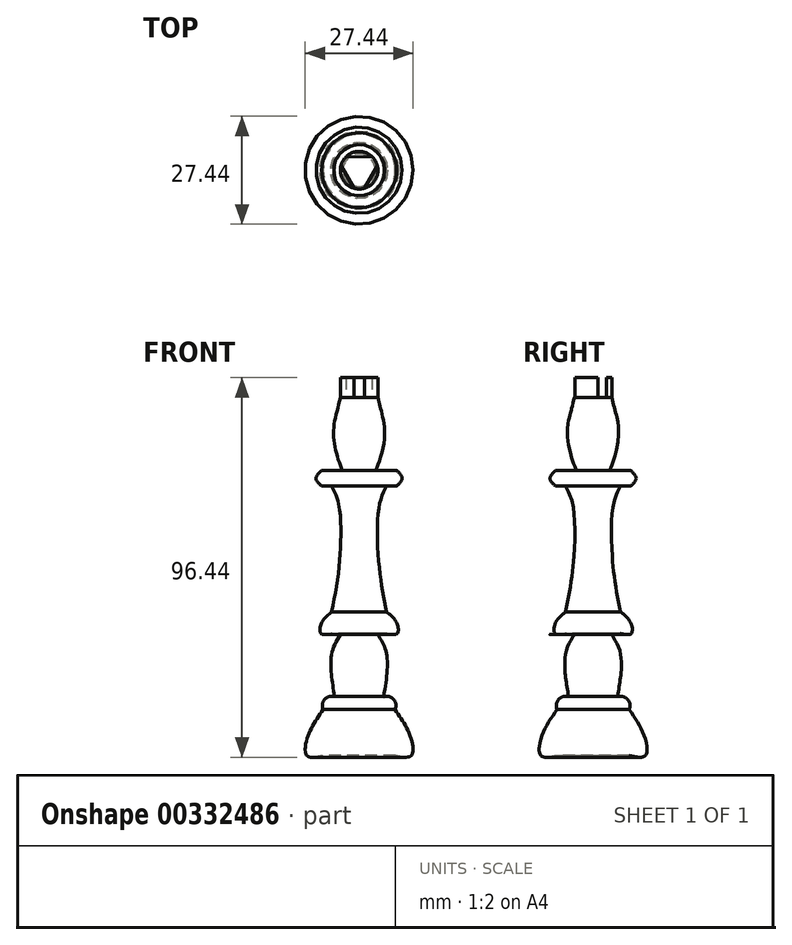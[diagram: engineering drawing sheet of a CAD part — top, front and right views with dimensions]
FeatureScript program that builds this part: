
annotation { "Feature Type Name" : "Feature", "Feature Type Description" : "" }
export const myFeature = defineFeature(function(context is Context, id is Id, definition is map)
    precondition{}
    {
        {
            var Q0;
            Q0=qCreatedBy(makeId("Front.planeOp"),FACE);
            var sketch = newSketch(context, id + "F0", { "sketchPlane" : qUnion([Q0])});
            skLineSegment(sketch, "E0.bottom", {"start": v(0, -66.55) * mm, "end": v(9.14, -66.55) * mm});
            skLineSegment(sketch, "E0.top", {"start": v(0, -54.86) * mm, "end": v(9.14, -54.86) * mm});
            skLineSegment(sketch, "E0.left", {"start": v(0, -66.55) * mm, "end": v(0, -54.86) * mm});
            skLineSegment(sketch, "E1.bottom", {"start": v(4.57, -54.86) * mm, "end": v(0, -54.86) * mm});
            skLineSegment(sketch, "E1.top", {"start": v(4.57, -35.56) * mm, "end": v(0, -35.56) * mm});
            skLineSegment(sketch, "E1.right", {"start": v(0, -54.86) * mm, "end": v(0, -35.56) * mm});
            skFitSpline(sketch, "E2", {"points": [v(9.14, -54.86) * mm, v(12.87, -61.24) * mm, v(13.29, -66.55) * mm, v(9.14, -66.55) * mm], "startDerivative": vector(10.89, -15.41) * mm, "endDerivative": vector(-17.8, 4.04) * mm});
            skLineSegment(sketch, "E3.bottom", {"start": v(0, -35.56) * mm, "end": v(6.97, -35.56) * mm});
            skLineSegment(sketch, "E3.top", {"start": v(0, -30.06) * mm, "end": v(6.97, -30.06) * mm});
            skLineSegment(sketch, "E3.left", {"start": v(0, -35.56) * mm, "end": v(0, -30.06) * mm});
            skPoint(sketch, "E4.1.internal.snap0", {"position": v(6.97, -32.8) * mm});
            skFitSpline(sketch, "E4", {"points": [v(6.97, -30.06) * mm, v(9.53, -32.8) * mm, v(9.69, -35.56) * mm, v(6.97, -35.56) * mm], "startDerivative": vector(8.1, -6.47) * mm, "endDerivative": vector(-10.67, 2.37) * mm});
            skFitSpline(sketch, "E5", {"points": [v(6.97, -30.06) * mm, v(5.1, -18.66) * mm, v(5.1, -3.15) * mm, v(6.97, 1.9) * mm], "startDerivative": vector(-6.05, 29.62) * mm, "endDerivative": vector(9.08, 17.3) * mm});
            skLineSegment(sketch, "E6.bottom", {"start": v(9.53, 1.9) * mm, "end": v(0, 1.9) * mm});
            skLineSegment(sketch, "E6.top", {"start": v(9.53, 5.86) * mm, "end": v(0, 5.86) * mm});
            skLineSegment(sketch, "E6.left", {"start": v(9.53, 1.9) * mm, "end": v(9.53, 5.86) * mm});
            skLineSegment(sketch, "E6.right", {"start": v(0, 1.9) * mm, "end": v(0, 5.86) * mm});
            skPoint(sketch, "E7.1.internal.snap0", {"position": v(9.53, 3.89) * mm});
            skFitSpline(sketch, "E7", {"points": [v(9.53, 5.86) * mm, v(10.95, 3.89) * mm, v(9.53, 1.9) * mm], "startDerivative": vector(4.27, -3.95) * mm, "endDerivative": vector(-4.27, -3.95) * mm});
            skLineSegment(sketch, "E8", {"start": v(0, 1.9) * mm, "end": v(0, -30.06) * mm});
            skLineSegment(sketch, "E9", {"start": v(0, 5.86) * mm, "end": v(0, 24.36) * mm});
            skLineSegment(sketch, "E10", {"start": v(0, -35.56) * mm, "end": v(0, -54.86) * mm});
            skLineSegment(sketch, "E11", {"start": v(0, -54.86) * mm, "end": v(4.57, -54.86) * mm});
            skLineSegment(sketch, "E12", {"start": v(0, -62.28) * mm, "end": v(0, -54.86) * mm});
            skLineSegment(sketch, "E13", {"start": v(0, 24.36) * mm, "end": v(0, 5.86) * mm});
            skLineSegment(sketch, "E14", {"start": v(0, 5.86) * mm, "end": v(0, 1.9) * mm});
            skLineSegment(sketch, "E15", {"start": v(0, -30.06) * mm, "end": v(0, -35.56) * mm});
            skLineSegment(sketch, "E16", {"start": v(0, -54.86) * mm, "end": v(0, -62.28) * mm});
            skLineSegment(sketch, "E17", {"start": v(0, -62.28) * mm, "end": v(0, -66.55) * mm});
            skArc(sketch, "E18", {"start": v(9.14, -54.86) * mm, "mid": v(8.75, -52.28) * mm, "end": v(6.22, -51.61) * mm});
            skFitSpline(sketch, "E19", {"points": [v(4.57, -35.56) * mm, v(7.01, -40.88) * mm, v(6.22, -51.61) * mm], "startDerivative": vector(7.26, -11.24) * mm, "endDerivative": vector(-3.43, -20.4) * mm});
            skFitSpline(sketch, "E20", {"points": [v(4.76, 24.36) * mm, v(5.55, 21.2) * mm, v(6.42, 13.8) * mm, v(4.12, 5.86) * mm, v(3.97, 5.86) * mm], "startDerivative": vector(3, -12.62) * mm, "endDerivative": vector(-2.58, 1.4) * mm});
            skLineSegment(sketch, "E21", {"start": v(0, 24.36) * mm, "end": v(4.76, 24.36) * mm});
            skLineSegment(sketch, "E22", {"start": v(0, 24.36) * mm, "end": v(0, -66.55) * mm});
            skSolve(sketch);
        }
        {
            var Q0;
            Q0 = qSketchRegion(id + "F0", true);
            var Q1;
            Q1=sQuery(id+"F0.wireOp",EDGE,"E8");
            revolve(context, id + "F1", {"entities" : qUnion([Q0]), "axis" : qUnion([Q1]), "revolveType" : RevolveType.FULL});
        }
        {
            var Q0;
            Q0=makeQuery(id+"F1.opRevolve","SWEPT_FACE",FACE,{"disambiguationData":[OSD([sQuery(id+"F0.wireOp",EDGE,"E21")])]});
            var sketch = newSketch(context, id + "F2", { "sketchPlane" : qUnion([Q0])});
            skArc(sketch, "E23", {"start": v(3.3, 3.45) * mm, "mid": v(-0.04, 4.8) * mm, "end": v(-3.35, 3.4) * mm});
            skLineSegment(sketch, "E24", {"start": v(-3.35, 3.4) * mm, "end": v(3.3, 3.45) * mm});
            skArc(sketch, "E25.1.0", {"start": v(-4.63, 1.13) * mm, "mid": v(-4.13, -2.43) * mm, "end": v(-1.26, -4.6) * mm});
            skLineSegment(sketch, "E25.1.1", {"start": v(-1.26, -4.6) * mm, "end": v(-4.63, 1.13) * mm});
            skArc(sketch, "E25.2.0", {"start": v(1.34, -4.57) * mm, "mid": v(4.18, -2.36) * mm, "end": v(4.6, 1.2) * mm});
            skLineSegment(sketch, "E25.2.1", {"start": v(4.6, 1.2) * mm, "end": v(1.34, -4.57) * mm});
            skPoint(sketch, "E25.center", {"position": v(0, 0) * mm});
            skSolve(sketch);
        }
        {
            var Q0;
            Q0 = qSketchRegion(id + "F2", true);
            extrude(context, id + "F3", {"entities" : qUnion([Q0]), "operationType" : NewBodyOperationType.ADD, "depth" : 5.08 * mm});
        }
    });
